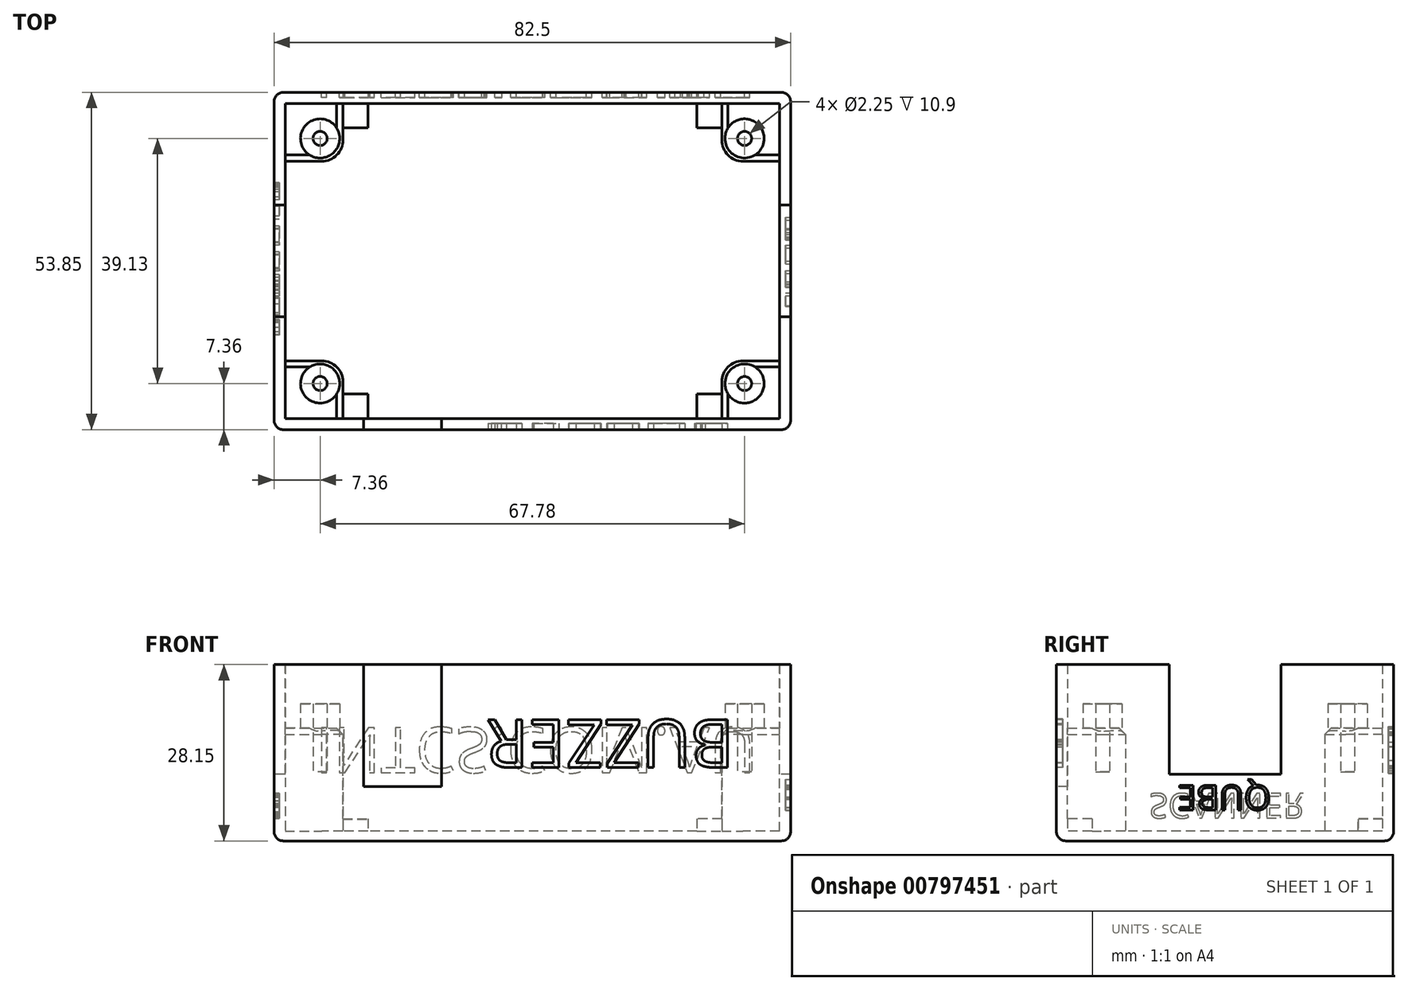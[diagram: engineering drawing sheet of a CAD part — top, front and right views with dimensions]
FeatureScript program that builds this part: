
annotation { "Feature Type Name" : "Feature", "Feature Type Description" : "" }
export const myFeature = defineFeature(function(context is Context, id is Id, definition is map)
    precondition{}
    {
        {
            var Q0;
            Q0=qCreatedBy(makeId("Top.planeOp"),FACE);
            var sketch = newSketch(context, id + "F0", { "sketchPlane" : qUnion([Q0])});
            skLineSegment(sketch, "E0.bottom", {"start": v(0, 0) * mm, "end": v(82.5, 0) * mm});
            skLineSegment(sketch, "E0.top", {"start": v(0, 53.85) * mm, "end": v(82.5, 53.85) * mm});
            skLineSegment(sketch, "E0.left", {"start": v(0, 0) * mm, "end": v(0, 53.85) * mm});
            skLineSegment(sketch, "E0.right", {"start": v(82.5, 0) * mm, "end": v(82.5, 53.85) * mm});
            skLineSegment(sketch, "E1.0", {"start": v(1.78, 1.78) * mm, "end": v(1.78, 52.07) * mm});
            skLineSegment(sketch, "E1.1", {"start": v(1.78, 1.78) * mm, "end": v(80.72, 1.78) * mm});
            skLineSegment(sketch, "E1.2", {"start": v(80.72, 1.78) * mm, "end": v(80.72, 52.07) * mm});
            skLineSegment(sketch, "E1.3", {"start": v(1.78, 52.07) * mm, "end": v(80.72, 52.07) * mm});
            skSolve(sketch);
        }
        {
            var Q0;
            Q0=qSketchRegion(id+"F0",true);
            extrude(context, id + "F1", {"entities" : qUnion([Q0]), "depth" : 28.15 * mm, "offsetDistance" : 25 * mm});
        }
        {
            var Q0;
            Q0=qCreatedBy(makeId("Front.planeOp"),FACE);
            var sketch = newSketch(context, id + "F2", { "sketchPlane" : qUnion([Q0])});
            skLineSegment(sketch, "E2.bottom", {"start": v(0, 0) * mm, "end": v(82.5, 0) * mm});
            skLineSegment(sketch, "E2.top", {"start": v(0, 1.55) * mm, "end": v(82.5, 1.55) * mm});
            skLineSegment(sketch, "E2.left", {"start": v(0, 0) * mm, "end": v(0, 1.55) * mm});
            skLineSegment(sketch, "E2.right", {"start": v(82.5, 0) * mm, "end": v(82.5, 1.55) * mm});
            skSolve(sketch);
        }
        {
            var Q0;
            Q0=qSketchRegion(id+"F2",true);
            extrude(context, id + "F3", {"entities" : qUnion([Q0]), "operationType" : NewBodyOperationType.ADD, "depth" : -53.85 * mm, "offsetDistance" : 25 * mm});
        }
        {
            var Q0;
            Q0=qCreatedBy(makeId("Top.planeOp"),FACE);
            var sketch = newSketch(context, id + "F4", { "sketchPlane" : qUnion([Q0])});
            skCircle(sketch, "E3", {"center": v(7.36, 7.36) * mm, "radius": 3.12 * mm});
            skCircle(sketch, "E4", {"center": v(7.36, 46.49) * mm, "radius": 3.12 * mm});
            skCircle(sketch, "E5", {"center": v(75.14, 7.36) * mm, "radius": 3.12 * mm});
            skCircle(sketch, "E6", {"center": v(75.14, 46.49) * mm, "radius": 3.12 * mm});
            skCircle(sketch, "E7.0", {"center": v(7.36, 7.36) * mm, "radius": 1.13 * mm});
            skCircle(sketch, "E8.0", {"center": v(7.36, 46.49) * mm, "radius": 1.13 * mm});
            skCircle(sketch, "E9.0", {"center": v(75.14, 46.49) * mm, "radius": 1.13 * mm});
            skCircle(sketch, "E10.0", {"center": v(75.14, 7.36) * mm, "radius": 1.13 * mm});
            skSolve(sketch);
        }
        {
            var Q0;
            Q0=makeQuery(id+"F4.imprint","IMPRINT",FACE,{"disambiguationData":[TD([[makeQuery(id+"F4.imprint","IMPRINT",EDGE,{"derivedFrom":sQuery(id+"F4.wireOp",EDGE,"E4")}),1.0]])]});
            var Q1;
            Q1=makeQuery(id+"F4.imprint","IMPRINT",FACE,{"disambiguationData":[TD([[makeQuery(id+"F4.imprint","IMPRINT",EDGE,{"derivedFrom":sQuery(id+"F4.wireOp",EDGE,"E3")}),1.0]])]});
            var Q2;
            Q2=makeQuery(id+"F4.imprint","IMPRINT",FACE,{"disambiguationData":[TD([[makeQuery(id+"F4.imprint","IMPRINT",EDGE,{"derivedFrom":sQuery(id+"F4.wireOp",EDGE,"E5")}),1.0]])]});
            var Q3;
            Q3=makeQuery(id+"F4.imprint","IMPRINT",FACE,{"disambiguationData":[TD([[makeQuery(id+"F4.imprint","IMPRINT",EDGE,{"derivedFrom":sQuery(id+"F4.wireOp",EDGE,"E6")}),1.0]])]});
            extrude(context, id + "F5", {"entities" : qUnion([Q0, Q1, Q2, Q3]), "operationType" : NewBodyOperationType.ADD, "depth" : 21.9 * mm, "offsetDistance" : 25 * mm});
        }
        {
            var Q0;
            Q0=qCreatedBy(makeId("Top.planeOp"),FACE);
            var sketch = newSketch(context, id + "F6", { "sketchPlane" : qUnion([Q0])});
            skLineSegment(sketch, "E11.bottom", {"start": v(0, 0) * mm, "end": v(11, 0) * mm});
            skLineSegment(sketch, "E11.left", {"start": v(0, 0) * mm, "end": v(0, 11) * mm});
            skLineSegment(sketch, "E12.top", {"start": v(0, 11) * mm, "end": v(7.62, 11) * mm});
            skLineSegment(sketch, "E12.right", {"start": v(11, 0) * mm, "end": v(11, 7.62) * mm});
            skPoint(sketch, "E13.visualSharp", {"position": v(11, 11) * mm});
            skArc(sketch, "E13.filletArc", {"start": v(11, 7.62) * mm, "mid": v(10.01, 10.01) * mm, "end": v(7.62, 11) * mm});
            skLineSegment(sketch, "E14.direction1", {"start": v(0, 0) * mm, "end": v(11, 0) * mm, "construction": true});
            skLineSegment(sketch, "E14.direction2", {"start": v(0, 0) * mm, "end": v(0, 11) * mm, "construction": true});
            skLineSegment(sketch, "E15.bottom", {"start": v(0, 0) * mm, "end": v(82.5, 0) * mm});
            skLineSegment(sketch, "E15.top", {"start": v(0, 53.85) * mm, "end": v(11, 53.85) * mm});
            skLineSegment(sketch, "E15.left", {"start": v(0, 0) * mm, "end": v(0, 53.85) * mm});
            skLineSegment(sketch, "E15.right", {"start": v(82.5, 0) * mm, "end": v(82.5, 11) * mm});
            skLineSegment(sketch, "E16.0.1.0", {"start": v(11, 53.85) * mm, "end": v(11, 46.23) * mm});
            skLineSegment(sketch, "E16.0.1.1", {"start": v(0, 53.85) * mm, "end": v(11, 53.85) * mm, "construction": true});
            skArc(sketch, "E16.0.1.2", {"start": v(7.62, 42.85) * mm, "mid": v(10.01, 43.84) * mm, "end": v(11, 46.23) * mm});
            skLineSegment(sketch, "E16.0.1.3", {"start": v(0, 53.85) * mm, "end": v(0, 42.85) * mm, "construction": true});
            skPoint(sketch, "E16.0.1.4", {"position": v(11, 42.85) * mm});
            skLineSegment(sketch, "E16.0.1.5", {"start": v(0, 42.85) * mm, "end": v(7.62, 42.85) * mm});
            skLineSegment(sketch, "E16.0.1.7", {"start": v(0, 53.85) * mm, "end": v(0, 42.85) * mm});
            skLineSegment(sketch, "E16.0.1.9", {"start": v(0, 53.85) * mm, "end": v(0, 42.85) * mm});
            skLineSegment(sketch, "E16.1.0.0", {"start": v(71.5, 0) * mm, "end": v(71.5, 7.62) * mm});
            skLineSegment(sketch, "E16.1.0.1", {"start": v(82.5, 0) * mm, "end": v(71.5, 0) * mm, "construction": true});
            skArc(sketch, "E16.1.0.2", {"start": v(74.88, 11) * mm, "mid": v(72.49, 10.01) * mm, "end": v(71.5, 7.62) * mm});
            skLineSegment(sketch, "E16.1.0.3", {"start": v(82.5, 0) * mm, "end": v(82.5, 11) * mm, "construction": true});
            skPoint(sketch, "E16.1.0.4", {"position": v(71.5, 11) * mm});
            skLineSegment(sketch, "E16.1.0.5", {"start": v(82.5, 11) * mm, "end": v(74.88, 11) * mm});
            skLineSegment(sketch, "E16.1.1.0", {"start": v(82.5, 42.85) * mm, "end": v(74.88, 42.85) * mm});
            skLineSegment(sketch, "E16.1.1.1", {"start": v(82.5, 53.85) * mm, "end": v(82.5, 42.85) * mm, "construction": true});
            skArc(sketch, "E16.1.1.2", {"start": v(71.5, 46.23) * mm, "mid": v(72.49, 43.84) * mm, "end": v(74.88, 42.85) * mm});
            skLineSegment(sketch, "E16.1.1.3", {"start": v(82.5, 53.85) * mm, "end": v(71.5, 53.85) * mm, "construction": true});
            skPoint(sketch, "E16.1.1.4", {"position": v(71.5, 42.85) * mm});
            skLineSegment(sketch, "E16.1.1.5", {"start": v(71.5, 53.85) * mm, "end": v(71.5, 46.23) * mm});
            skLineSegment(sketch, "E16.1.1.6", {"start": v(82.5, 53.85) * mm, "end": v(82.5, 42.85) * mm});
            skLineSegment(sketch, "E16.1.1.7", {"start": v(82.5, 53.85) * mm, "end": v(71.5, 53.85) * mm});
            skLineSegment(sketch, "E16.1.1.8", {"start": v(82.5, 53.85) * mm, "end": v(82.5, 42.85) * mm});
            skLineSegment(sketch, "E16.1.1.9", {"start": v(82.5, 53.85) * mm, "end": v(71.5, 53.85) * mm});
            skLineSegment(sketch, "E17.trimOffspring", {"start": v(71.5, 53.85) * mm, "end": v(82.5, 53.85) * mm});
            skLineSegment(sketch, "E18.trimOffspring", {"start": v(0, 42.85) * mm, "end": v(0, 53.85) * mm, "construction": true});
            skLineSegment(sketch, "E19.trimOffspring", {"start": v(71.5, 0) * mm, "end": v(82.5, 0) * mm, "construction": true});
            skLineSegment(sketch, "E20.trimOffspring", {"start": v(82.5, 42.85) * mm, "end": v(82.5, 53.85) * mm});
            skSolve(sketch);
        }
        {
            var Q0;
            Q0=qSketchRegion(id+"F6",true);
            extrude(context, id + "F7", {"entities" : qUnion([Q0]), "operationType" : NewBodyOperationType.ADD, "depth" : 18 * mm, "offsetDistance" : 25 * mm});
        }
        {
            var Q0;
            Q0=makeQuery(id+"F3.boolean.opBoolean","MERGE",FACE,{"derivedFrom":[makeQuery(id+"F1.opExtrude","CAP_FACE",FACE,{"disambiguationData":[OSD([sQuery(id+"F0.wireOp",EDGE,"E0.bottom"),sQuery(id+"F0.wireOp",EDGE,"E0.top"),sQuery(id+"F0.wireOp",EDGE,"E0.left"),sQuery(id+"F0.wireOp",EDGE,"E0.right"),sQuery(id+"F0.wireOp",EDGE,"E1.0"),sQuery(id+"F0.wireOp",EDGE,"E1.1"),sQuery(id+"F0.wireOp",EDGE,"E1.2"),sQuery(id+"F0.wireOp",EDGE,"E1.3")])],"isStart":true}),makeQuery(id+"F3.opExtrude","SWEPT_FACE",FACE,{"disambiguationData":[OSD([sQuery(id+"F2.wireOp",EDGE,"E2.bottom")])]})]});
            var Q1;
            Q1=makeQuery(id+"F1.opExtrude","SWEPT_EDGE",EDGE,{"disambiguationData":[OSD([sQuery(id+"F0.wireOp",EDGE,"E0.top"),sQuery(id+"F0.wireOp",EDGE,"E0.right")])]});
            var Q2;
            Q2=makeQuery(id+"F1.opExtrude","SWEPT_EDGE",EDGE,{"disambiguationData":[OSD([sQuery(id+"F0.wireOp",EDGE,"E0.bottom"),sQuery(id+"F0.wireOp",EDGE,"E0.right")])]});
            var Q3;
            Q3=makeQuery(id+"F1.opExtrude","SWEPT_EDGE",EDGE,{"disambiguationData":[OSD([sQuery(id+"F0.wireOp",EDGE,"E0.bottom"),sQuery(id+"F0.wireOp",EDGE,"E0.left")])]});
            var Q4;
            Q4=makeQuery(id+"F1.opExtrude","SWEPT_EDGE",EDGE,{"disambiguationData":[OSD([sQuery(id+"F0.wireOp",EDGE,"E0.top"),sQuery(id+"F0.wireOp",EDGE,"E0.left")])]});
            fillet(context, id + "F8", {"entities" : qUnion([Q0, Q1, Q2, Q3, Q4]), "radius" : 1.5 * mm, "tangentPropagation" : true, "allowEdgeOverflow" : false});
        }
        {
            var Q0;
            Q0=makeQuery(id+"F7.opExtrude","CAP_EDGE",EDGE,{"disambiguationData":[OSD([sQuery(id+"F6.wireOp",EDGE,"E16.0.1.0")])],"isStart":false});
            var Q1;
            Q1=makeQuery(id+"F7.opExtrude","CAP_EDGE",EDGE,{"disambiguationData":[OSD([sQuery(id+"F6.wireOp",EDGE,"E16.0.1.5")])],"isStart":false});
            var Q2;
            Q2=makeQuery(id+"F7.opExtrude","CAP_EDGE",EDGE,{"disambiguationData":[OSD([sQuery(id+"F6.wireOp",EDGE,"E12.top")])],"isStart":false});
            var Q3;
            Q3=makeQuery(id+"F7.opExtrude","CAP_EDGE",EDGE,{"disambiguationData":[OSD([sQuery(id+"F6.wireOp",EDGE,"E12.right")])],"isStart":false});
            var Q4;
            Q4=makeQuery(id+"F7.opExtrude","CAP_EDGE",EDGE,{"disambiguationData":[OSD([sQuery(id+"F6.wireOp",EDGE,"E16.1.0.0")])],"isStart":false});
            var Q5;
            Q5=makeQuery(id+"F7.opExtrude","CAP_EDGE",EDGE,{"disambiguationData":[OSD([sQuery(id+"F6.wireOp",EDGE,"E16.1.0.5")])],"isStart":false});
            var Q6;
            Q6=makeQuery(id+"F7.opExtrude","CAP_EDGE",EDGE,{"disambiguationData":[OSD([sQuery(id+"F6.wireOp",EDGE,"E16.1.1.5")])],"isStart":false});
            var Q7;
            Q7=makeQuery(id+"F7.opExtrude","CAP_EDGE",EDGE,{"disambiguationData":[OSD([sQuery(id+"F6.wireOp",EDGE,"E16.1.1.0")])],"isStart":false});
            var Q8;
            Q8=makeQuery(id+"F7.opExtrude","CAP_EDGE",EDGE,{"disambiguationData":[OSD([sQuery(id+"F6.wireOp",EDGE,"E13.filletArc")])],"isStart":false});
            var Q9;
            Q9=makeQuery(id+"F7.opExtrude","CAP_EDGE",EDGE,{"disambiguationData":[OSD([sQuery(id+"F6.wireOp",EDGE,"E16.0.1.2")])],"isStart":false});
            var Q10;
            Q10=makeQuery(id+"F7.opExtrude","CAP_EDGE",EDGE,{"disambiguationData":[OSD([sQuery(id+"F6.wireOp",EDGE,"E16.1.1.2")])],"isStart":false});
            var Q11;
            Q11=makeQuery(id+"F7.opExtrude","CAP_EDGE",EDGE,{"disambiguationData":[OSD([sQuery(id+"F6.wireOp",EDGE,"E16.1.0.2")])],"isStart":false});
            chamfer(context, id + "F9", {"entities" : qUnion([Q0, Q1, Q2, Q3, Q4, Q5, Q6, Q7, Q8, Q9, Q10, Q11]), "width" : 1 * mm});
        }
        {
            var Q0;
            Q0=makeQuery(id+"F7.boolean.opBoolean","SPLIT",FACE,{"disambiguationData":[TD([makeQuery(id+"F5.opExtrude","SWEPT_FACE",FACE,{"disambiguationData":[OSD([sQuery(id+"F4.wireOp",EDGE,"E7.0")])]})])],"derivedFrom":makeQuery(id+"F7.opExtrude","CAP_FACE",FACE,{"disambiguationData":[OSD([sQuery(id+"F6.wireOp",EDGE,"E12.top"),sQuery(id+"F6.wireOp",EDGE,"E12.right"),sQuery(id+"F6.wireOp",EDGE,"E13.filletArc"),sQuery(id+"F6.wireOp",EDGE,"E15.bottom"),sQuery(id+"F6.wireOp",EDGE,"E15.left")])],"isStart":false})});
            var Q1;
            Q1=makeQuery(id+"F7.boolean.opBoolean","SPLIT",FACE,{"disambiguationData":[TD([makeQuery(id+"F5.opExtrude","SWEPT_FACE",FACE,{"disambiguationData":[OSD([sQuery(id+"F4.wireOp",EDGE,"E8.0")])]})])],"derivedFrom":makeQuery(id+"F7.opExtrude","CAP_FACE",FACE,{"disambiguationData":[OSD([sQuery(id+"F6.wireOp",EDGE,"E16.0.1.0"),sQuery(id+"F6.wireOp",EDGE,"E16.0.1.2"),sQuery(id+"F6.wireOp",EDGE,"E16.0.1.5"),sQuery(id+"F6.wireOp",EDGE,"E15.top"),sQuery(id+"F6.wireOp",EDGE,"E16.0.1.9")])],"isStart":false})});
            var Q2;
            Q2=makeQuery(id+"F7.boolean.opBoolean","SPLIT",FACE,{"disambiguationData":[TD([makeQuery(id+"F5.opExtrude","SWEPT_FACE",FACE,{"disambiguationData":[OSD([sQuery(id+"F4.wireOp",EDGE,"E9.0")])]})])],"derivedFrom":makeQuery(id+"F7.opExtrude","CAP_FACE",FACE,{"disambiguationData":[OSD([sQuery(id+"F6.wireOp",EDGE,"E16.1.1.0"),sQuery(id+"F6.wireOp",EDGE,"E16.1.1.2"),sQuery(id+"F6.wireOp",EDGE,"E16.1.1.5"),sQuery(id+"F6.wireOp",EDGE,"E17.trimOffspring"),sQuery(id+"F6.wireOp",EDGE,"E20.trimOffspring")])],"isStart":false})});
            var Q3;
            Q3=makeQuery(id+"F7.boolean.opBoolean","SPLIT",FACE,{"disambiguationData":[TD([makeQuery(id+"F5.opExtrude","SWEPT_FACE",FACE,{"disambiguationData":[OSD([sQuery(id+"F4.wireOp",EDGE,"E10.0")])]})])],"derivedFrom":makeQuery(id+"F7.opExtrude","CAP_FACE",FACE,{"disambiguationData":[OSD([sQuery(id+"F6.wireOp",EDGE,"E15.bottom"),sQuery(id+"F6.wireOp",EDGE,"E16.1.0.0"),sQuery(id+"F6.wireOp",EDGE,"E16.1.0.2"),sQuery(id+"F6.wireOp",EDGE,"E16.1.0.5"),sQuery(id+"F6.wireOp",EDGE,"E15.right")])],"isStart":false})});
            extrude(context, id + "F10", {"entities" : qUnion([Q0, Q1, Q2, Q3]), "operationType" : NewBodyOperationType.REMOVE, "oppositeDirection" : true, "depth" : 7 * mm, "offsetDistance" : 25 * mm});
        }
        {
            var Q0;
            Q0=qCreatedBy(makeId("Right.planeOp"),FACE);
            var sketch = newSketch(context, id + "F11", { "sketchPlane" : qUnion([Q0])});
            skLineSegment(sketch, "E21.bottom", {"start": v(18, 10.65) * mm, "end": v(35.85, 10.65) * mm});
            skLineSegment(sketch, "E21.top", {"start": v(18, 28.15) * mm, "end": v(35.85, 28.15) * mm});
            skLineSegment(sketch, "E21.left", {"start": v(18, 10.65) * mm, "end": v(18, 28.15) * mm});
            skLineSegment(sketch, "E21.right", {"start": v(35.85, 10.65) * mm, "end": v(35.85, 28.15) * mm});
            skSolve(sketch);
        }
        {
            var Q0;
            Q0=makeQuery(id+"F11.imprint","IMPRINT",FACE,{"disambiguationData":[TD([[makeQuery(id+"F11.imprint","IMPRINT",EDGE,{"derivedFrom":sQuery(id+"F11.wireOp",EDGE,"E21.bottom")}),1.0]])]});
            extrude(context, id + "F12", {"entities" : qUnion([Q0]), "operationType" : NewBodyOperationType.REMOVE, "depth" : 137.9 * mm, "offsetDistance" : 25 * mm});
        }
        {
            var Q0;
            Q0=qCreatedBy(makeId("Front.planeOp"),FACE);
            var sketch = newSketch(context, id + "F13", { "sketchPlane" : qUnion([Q0])});
            skLineSegment(sketch, "E22.bottom", {"start": v(14.28, 8.65) * mm, "end": v(26.78, 8.65) * mm});
            skLineSegment(sketch, "E22.top", {"start": v(14.28, 28.15) * mm, "end": v(26.78, 28.15) * mm});
            skLineSegment(sketch, "E22.left", {"start": v(14.28, 8.65) * mm, "end": v(14.28, 28.15) * mm});
            skLineSegment(sketch, "E22.right", {"start": v(26.78, 8.65) * mm, "end": v(26.78, 28.15) * mm});
            skSolve(sketch);
        }
        {
            var Q0;
            Q0=qSketchRegion(id+"F13",true);
            extrude(context, id + "F14", {"entities" : qUnion([Q0]), "operationType" : NewBodyOperationType.REMOVE, "oppositeDirection" : true, "depth" : 25 * mm, "offsetDistance" : 25 * mm});
        }
        {
            var Q0;
            Q0=makeQuery(id+"F1.opExtrude","SWEPT_FACE",FACE,{"disambiguationData":[OSD([sQuery(id+"F0.wireOp",EDGE,"E0.top")])]});
            var sketch = newSketch(context, id + "F15", { "sketchPlane" : qUnion([Q0])});
            skText(sketch, "E23", { "text": "INTCS.COM.AU", "fontName": "OpenSans-Regular.ttf"});
            const initialGuessF15  = {"E23": [-0.0066, 0.0181, -1, 0, 0.00726]};
            skSetInitialGuess(sketch, initialGuessF15);
            skSolve(sketch);
        }
        {
            var Q0;
            Q0=qSketchRegion(id+"F15",true);
            extrude(context, id + "F16", {"entities" : qUnion([Q0]), "operationType" : NewBodyOperationType.REMOVE, "oppositeDirection" : true, "depth" : 0.85 * mm, "offsetDistance" : 25 * mm});
        }
        {
            var Q0;
            Q0=makeQuery(id+"F1.opExtrude","SWEPT_FACE",FACE,{"disambiguationData":[OSD([sQuery(id+"F0.wireOp",EDGE,"E0.left")])]});
            var sketch = newSketch(context, id + "F17", { "sketchPlane" : qUnion([Q0])});
            skText(sketch, "E24", { "text": "SCANNER", "fontName": "OpenSans-Regular.ttf"});
            const initialGuessF17  = {"E24": [-0.0148, 0.00757, -1, 0, 0.00396]};
            skSetInitialGuess(sketch, initialGuessF17);
            skSolve(sketch);
        }
        {
            var Q0;
            Q0=makeQuery(id+"F1.opExtrude","SWEPT_FACE",FACE,{"disambiguationData":[OSD([sQuery(id+"F0.wireOp",EDGE,"E0.right")])]});
            var sketch = newSketch(context, id + "F18", { "sketchPlane" : qUnion([Q0])});
            skText(sketch, "E25", { "text": "QUBE", "fontName": "OpenSans-Regular.ttf"});
            const initialGuessF18  = {"E25": [0.03424, 0.00887, -1, 0, 0.00396]};
            skSetInitialGuess(sketch, initialGuessF18);
            skSolve(sketch);
        }
        {
            var Q0;
            Q0=qSketchRegion(id+"F18",true);
            extrude(context, id + "F19", {"entities" : qUnion([Q0]), "operationType" : NewBodyOperationType.REMOVE, "oppositeDirection" : true, "depth" : .85 * mm, "offsetDistance" : 25 * mm});
        }
        {
            var Q0;
            Q0=qSketchRegion(id+"F17",true);
            extrude(context, id + "F20", {"entities" : qUnion([Q0]), "operationType" : NewBodyOperationType.REMOVE, "oppositeDirection" : true, "depth" : .85 * mm, "offsetDistance" : 25 * mm});
        }
        {
            var Q0;
            Q0=qCreatedBy(makeId("Right.planeOp"),FACE);
            var sketch = newSketch(context, id + "F21", { "sketchPlane" : qUnion([Q0])});
            skLineSegment(sketch, "E26", {"start": v(48.18, 3.5) * mm, "end": v(52.35, 3.5) * mm});
            skLineSegment(sketch, "E27", {"start": v(52.35, 3.5) * mm, "end": v(52.35, 1.5) * mm});
            skLineSegment(sketch, "E28", {"start": v(52.35, 1.5) * mm, "end": v(48.18, 1.5) * mm});
            skLineSegment(sketch, "E29", {"start": v(48.18, 1.5) * mm, "end": v(48.18, 3.5) * mm});
            skLineSegment(sketch, "E30", {"start": v(5.68, 1.5) * mm, "end": v(1.5, 1.5) * mm});
            skLineSegment(sketch, "E31", {"start": v(1.5, 1.5) * mm, "end": v(1.5, 3.5) * mm});
            skLineSegment(sketch, "E32", {"start": v(1.5, 3.5) * mm, "end": v(5.68, 3.5) * mm});
            skLineSegment(sketch, "E33", {"start": v(5.68, 3.5) * mm, "end": v(5.68, 1.5) * mm});
            skSolve(sketch);
        }
        {
            var Q0;
            Q0=qSketchRegion(id+"F21",true);
            extrude(context, id + "F22", {"entities" : qUnion([Q0]), "operationType" : NewBodyOperationType.ADD, "depth" : 15 * mm, "offsetDistance" : 25 * mm});
        }
        {
            var Q0;
            {var subQ1=sQuery(id+"F0.wireOp",EDGE,"E0.right");var subQ5=makeQuery(id+"F1.opExtrude","SWEPT_FACE",FACE,{"disambiguationData":[OSD([subQ1])]});Q0=makeQuery(id+"F19.boolean.opBoolean","SPLIT",FACE,{"disambiguationData":[TD([makeQuery(id+"F8.opFillet","BLEND_FACE",FACE,{"disambiguationData":[OSD([subQ1])]})])],"derivedFrom":subQ5});}
            var sketch = newSketch(context, id + "F23", { "sketchPlane" : qUnion([Q0])});
            skLineSegment(sketch, "E34.top", {"start": v(1.5, 3.5) * mm, "end": v(5.67, 3.5) * mm});
            skLineSegment(sketch, "E34.right", {"start": v(5.67, 1.5) * mm, "end": v(5.67, 3.5) * mm});
            skLineSegment(sketch, "E35.top", {"start": v(52.35, 3.5) * mm, "end": v(48.18, 3.5) * mm});
            skLineSegment(sketch, "E35.right", {"start": v(48.17, 1.5) * mm, "end": v(48.17, 3.5) * mm});
            skLineSegment(sketch, "E36", {"start": v(1.5, 3.5) * mm, "end": v(1.5, 1.5) * mm});
            skLineSegment(sketch, "E37", {"start": v(1.5, 1.5) * mm, "end": v(5.67, 1.5) * mm});
            skPoint(sketch, "E34.left.start.orphan", {"position": v(0, 0) * mm});
            skLineSegment(sketch, "E38", {"start": v(52.35, 3.5) * mm, "end": v(52.35, 1.5) * mm});
            skLineSegment(sketch, "E39", {"start": v(52.35, 1.5) * mm, "end": v(48.18, 1.5) * mm});
            skPoint(sketch, "E35.bottom.start.orphan", {"position": v(53.85, 0) * mm});
            skSolve(sketch);
        }
        {
            var Q0;
            Q0=qSketchRegion(id+"F23",true);
            extrude(context, id + "F24", {"entities" : qUnion([Q0]), "operationType" : NewBodyOperationType.ADD, "depth" : -15 * mm, "offsetDistance" : 25 * mm});
        }
        {
            var Q0;
            Q0=makeQuery(id+"F1.opExtrude","SWEPT_FACE",FACE,{"disambiguationData":[OSD([sQuery(id+"F0.wireOp",EDGE,"E0.bottom")])]});
            var sketch = newSketch(context, id + "F25", { "sketchPlane" : qUnion([Q0])});
            skText(sketch, "E40", { "text": "BUZZER\n", "fontName": "OpenSans-Regular.ttf"});
            const initialGuessF25  = {"E40": [0.07348, 0.01935, -1, 0, 0.0077]};
            skSetInitialGuess(sketch, initialGuessF25);
            skSolve(sketch);
        }
        {
            var Q0;
            Q0=qSketchRegion(id+"F25",true);
            extrude(context, id + "F26", {"entities" : qUnion([Q0]), "operationType" : NewBodyOperationType.REMOVE, "oppositeDirection" : true, "depth" : 1 * mm, "offsetDistance" : 25 * mm});
        }
    });
